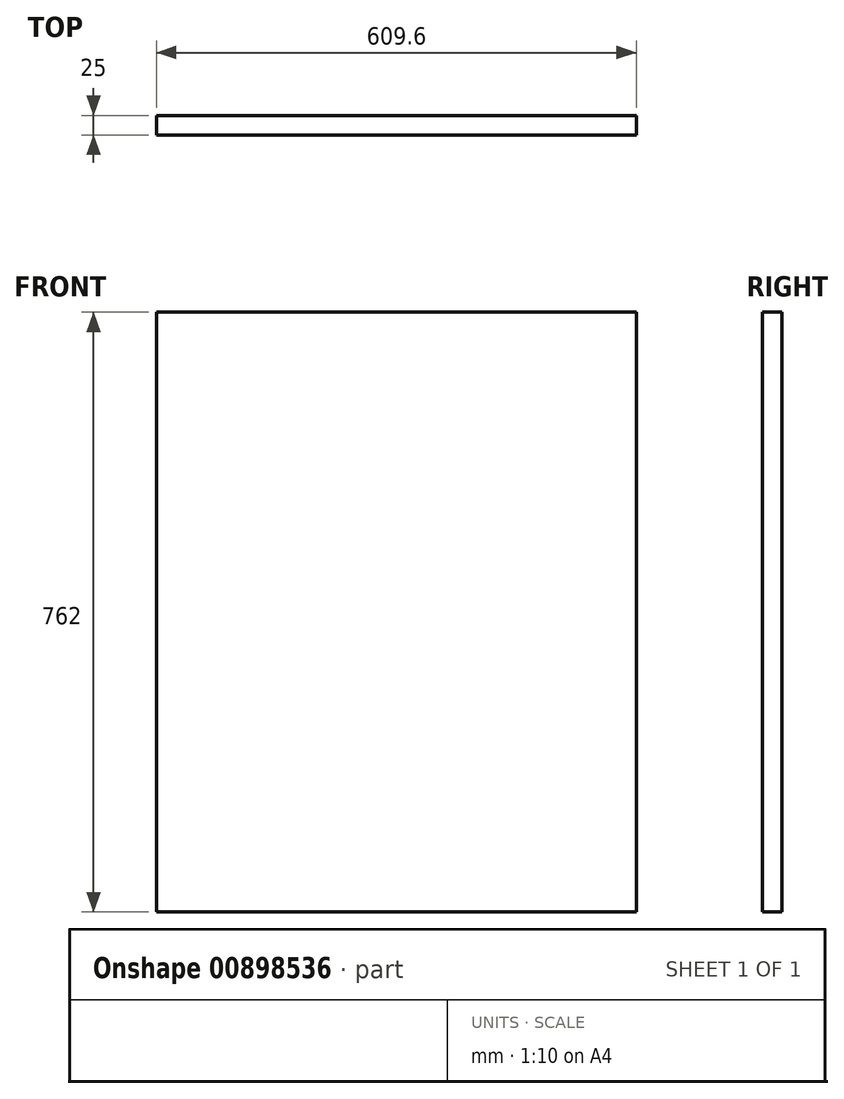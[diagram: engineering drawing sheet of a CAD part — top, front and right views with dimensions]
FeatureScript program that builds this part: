
annotation { "Feature Type Name" : "Feature", "Feature Type Description" : "" }
export const myFeature = defineFeature(function(context is Context, id is Id, definition is map)
    precondition{}
    {
        {
            var Q0;
            Q0=qCreatedBy(makeId("Front.planeOp"),FACE);
            var sketch = newSketch(context, id + "F0", { "sketchPlane" : qUnion([Q0])});
            skLineSegment(sketch, "E0.bottom", {"start": v(-62.84, 48.12) * mm, "end": v(546.76, 48.12) * mm});
            skLineSegment(sketch, "E0.top", {"start": v(-62.84, -713.88) * mm, "end": v(546.76, -713.88) * mm});
            skLineSegment(sketch, "E0.left", {"start": v(-62.84, 48.12) * mm, "end": v(-62.84, -713.88) * mm});
            skLineSegment(sketch, "E0.right", {"start": v(546.76, 48.12) * mm, "end": v(546.76, -713.88) * mm});
            skSolve(sketch);
        }
        {
            var Q0;
            Q0=makeQuery(id+"F0.imprint","IMPRINT",FACE,{"disambiguationData":[TD([[makeQuery(id+"F0.imprint","IMPRINT",EDGE,{"derivedFrom":sQuery(id+"F0.wireOp",EDGE,"E0.bottom")}),-1.0]])]});
            extrude(context, id + "F1", {"entities" : qUnion([Q0]), "depth" : 25 * mm, "offsetDistance" : 25 * mm});
        }
    });
